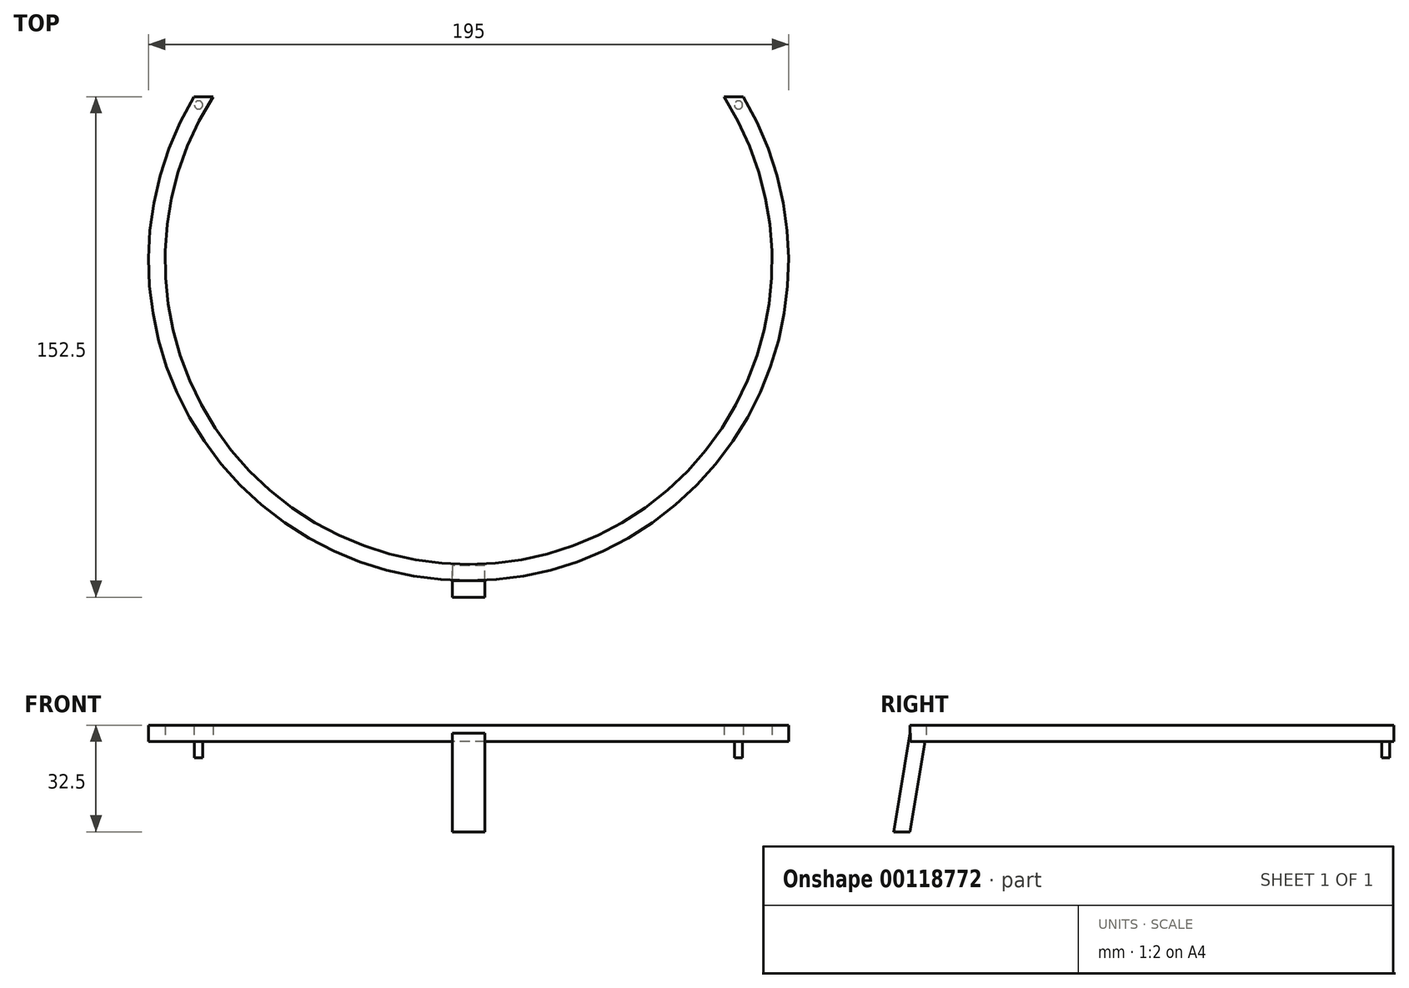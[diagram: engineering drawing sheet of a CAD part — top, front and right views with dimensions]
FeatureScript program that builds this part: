
annotation { "Feature Type Name" : "Feature", "Feature Type Description" : "" }
export const myFeature = defineFeature(function(context is Context, id is Id, definition is map)
    precondition{}
    {
        {
            var Q0;
            Q0=qCreatedBy(makeId("Top.planeOp"),FACE);
            var sketch = newSketch(context, id + "F0", { "sketchPlane" : qUnion([Q0])});
            skCircle(sketch, "E0", {"center": v(0, 0) * mm, "radius": 97.5 * mm});
            skCircle(sketch, "E1", {"center": v(0, 0) * mm, "radius": 92.5 * mm});
            skSolve(sketch);
        }
        {
            var Q0;
            Q0 = qSketchRegion(id + "F0", true);
            extrude(context, id + "F1", {"entities" : qUnion([Q0]), "depth" : 5 * mm});
        }
        {
            var Q0;
            Q0=qCreatedBy(makeId("Right.planeOp"),FACE);
            var sketch = newSketch(context, id + "F2", { "sketchPlane" : qUnion([Q0])});
            skPoint(sketch, "E2", {"position": v(-95, 2.5) * mm});
            skLineSegment(sketch, "E3", {"start": v(-95, 2.5) * mm, "end": v(-100, -27.5) * mm});
            skSolve(sketch);
        }
        {
            var Q0;
            Q0=sQuery(id+"F2.wireOp",VERTEX,"E3.end");
            var Q1;
            Q1=qCreatedBy(makeId("Top.planeOp"),FACE);
            cPlane(context, id + "F3", {"entities" : qUnion([Q0, Q1]), "cplaneType" : CPlaneType.PLANE_POINT, "offset" : 25 * mm, "width" : 150 * mm, "height" : 150 * mm});
        }
        {
            var Q0;
            Q0=qCreatedBy(id+"F3.planeOp",FACE);
            var sketch = newSketch(context, id + "F4", { "sketchPlane" : qUnion([Q0])});
            skPoint(sketch, "E4", {"position": v(0, -100) * mm});
            skLineSegment(sketch, "E5.bottom", {"start": v(5, -102.5) * mm, "end": v(-5, -102.5) * mm});
            skLineSegment(sketch, "E5.top", {"start": v(5, -97.5) * mm, "end": v(-5, -97.5) * mm});
            skLineSegment(sketch, "E5.left", {"start": v(5, -102.5) * mm, "end": v(5, -97.5) * mm});
            skLineSegment(sketch, "E5.right", {"start": v(-5, -102.5) * mm, "end": v(-5, -97.5) * mm});
            skSolve(sketch);
        }
        {
            var Q0;
            Q0=makeQuery(id+"F4.imprint","IMPRINT",FACE,{"disambiguationData":[TD([[makeQuery(id+"F4.imprint","IMPRINT",EDGE,{"derivedFrom":sQuery(id+"F4.wireOp",EDGE,"E5.bottom")}),-1.0]])]});
            var Q1;
            Q1=sQuery(id+"F2.wireOp",EDGE,"E3");
            sweep(context, id + "F5", {"operationType" : NewBodyOperationType.ADD, "profiles" : qUnion([Q0]), "path" : qUnion([Q1])});
        }
        {
            var Q0;
            Q0=makeQuery(id+"F1.opExtrude","CAP_FACE",FACE,{"disambiguationData":[OSD([sQuery(id+"F0.wireOp",EDGE,"E0"),sQuery(id+"F0.wireOp",EDGE,"E1")])],"isStart":true});
            var sketch = newSketch(context, id + "F6", { "sketchPlane" : qUnion([Q0])});
            skLineSegment(sketch, "E6", {"start": v(0, 0) * mm, "end": v(-74.69, -62.67) * mm});
            skLineSegment(sketch, "E7", {"start": v(0, 0) * mm, "end": v(-91.62, -33.35) * mm});
            skLineSegment(sketch, "E8.MirrorCS", {"start": v(0, 0) * mm, "end": v(74.69, -62.67) * mm});
            skLineSegment(sketch, "E9.MirrorCS", {"start": v(0, 0) * mm, "end": v(91.62, -33.35) * mm});
            skSolve(sketch);
        }
        {
            var Q0;
            {var subQ0=sQuery(id+"F6.wireOp",EDGE,"E6");var subQ1=makeQuery(id+"F1.opExtrude","CAP_EDGE",EDGE,{"disambiguationData":[OSD([sQuery(id+"F0.wireOp",EDGE,"E0")])],"isStart":true});var subQ2=makeQuery(id+"F6.imprint","INTERSECT",VERTEX,{"derivedFrom":[subQ1,subQ0]});Q0=makeQuery(id+"F6.imprint","IMPRINT",FACE,{"disambiguationData":[TD([[makeQuery(id+"F6.imprint","IMPRINT",EDGE,{"disambiguationData":[TD([[subQ2,1.0]])],"derivedFrom":subQ0}),-1.0]])]});}
            var Q1;
            {var subQ0=sQuery(id+"F6.wireOp",EDGE,"E8.MirrorCS");var subQ1=makeQuery(id+"F1.opExtrude","CAP_EDGE",EDGE,{"disambiguationData":[OSD([sQuery(id+"F0.wireOp",EDGE,"E0")])],"isStart":true});var subQ2=makeQuery(id+"F6.imprint","INTERSECT",VERTEX,{"derivedFrom":[subQ1,subQ0]});Q1=makeQuery(id+"F6.imprint","IMPRINT",FACE,{"disambiguationData":[TD([[makeQuery(id+"F6.imprint","IMPRINT",EDGE,{"disambiguationData":[TD([[subQ2,1.0]])],"derivedFrom":subQ0}),1.0]])]});}
            extrude(context, id + "F7", {"entities" : qUnion([Q0, Q1]), "operationType" : NewBodyOperationType.ADD, "depth" : 27.5 * mm});
        }
        {
            var Q0;
            Q0=qCreatedBy(makeId("Right.planeOp"),FACE);
            cPlane(context, id + "F8", {"entities" : qUnion([Q0]), "cplaneType" : CPlaneType.OFFSET, "offset" : 100 * mm, "width" : 150 * mm, "height" : 150 * mm});
        }
        {
            var Q0;
            Q0=qCreatedBy(id+"F8.planeOp",FACE);
            var sketch = newSketch(context, id + "F9", { "sketchPlane" : qUnion([Q0])});
            skLineSegment(sketch, "E10", {"start": v(0, 0) * mm, "end": v(50, 0) * mm});
            skLineSegment(sketch, "E11", {"start": v(50, 0) * mm, "end": v(50, 5) * mm});
            skLineSegment(sketch, "E12", {"start": v(50, 5) * mm, "end": v(101.86, 5) * mm});
            skLineSegment(sketch, "E13", {"start": v(101.86, 5) * mm, "end": v(101.86, -29.5) * mm});
            skLineSegment(sketch, "E14", {"start": v(101.86, -29.5) * mm, "end": v(0, -29.5) * mm});
            skLineSegment(sketch, "E15", {"start": v(0, -29.5) * mm, "end": v(0, 0) * mm});
            skLineSegment(sketch, "E16", {"start": v(50, 5) * mm, "end": v(-137.03, 5) * mm});
            skLineSegment(sketch, "E17", {"start": v(-137.03, 5) * mm, "end": v(-137.03, -29.5) * mm});
            skLineSegment(sketch, "E18", {"start": v(-137.03, -29.5) * mm, "end": v(0, -29.5) * mm});
            skSolve(sketch);
        }
        {
            var Q0;
            Q0=makeQuery(id+"F9.imprint","IMPRINT",FACE,{"disambiguationData":[TD([[makeQuery(id+"F9.imprint","IMPRINT",EDGE,{"derivedFrom":sQuery(id+"F9.wireOp",EDGE,"E10")}),-1.0]])]});
            extrude(context, id + "F10", {"entities" : qUnion([Q0]), "operationType" : NewBodyOperationType.REMOVE, "endBound" : BoundingType.THROUGH_ALL, "oppositeDirection" : true, "depth" : 25 * mm});
        }
        {
            var Q0;
            {var subQ2=sQuery(id+"F0.wireOp",EDGE,"E0");var subQ4=sQuery(id+"F6.wireOp",EDGE,"E7");var subQ6=sQuery(id+"F0.wireOp",EDGE,"E1");Q0=makeQuery(id+"F10.boolean.opBoolean","MERGE",FACE,{"derivedFrom":[makeQuery(id+"F7.boolean.opBoolean","SPLIT",FACE,{"disambiguationData":[TD([makeQuery(id+"F7.opExtrude","SWEPT_FACE",FACE,{"disambiguationData":[OSD([subQ4])]})])],"derivedFrom":makeQuery(id+"F1.opExtrude","CAP_FACE",FACE,{"disambiguationData":[OSD([subQ2,subQ6])],"isStart":true})}),makeQuery(id+"F10.opExtrude","SWEPT_FACE",FACE,{"disambiguationData":[OSD([sQuery(id+"F9.wireOp",EDGE,"E10")])]})]});}
            var sketch = newSketch(context, id + "F11", { "sketchPlane" : qUnion([Q0])});
            skPoint(sketch, "E19", {"position": v(82.26, -47.5) * mm});
            skLineSegment(sketch, "E20", {"start": v(85.15, -47.5) * mm, "end": v(79.37, -47.5) * mm, "construction": true});
            skCircle(sketch, "E21", {"center": v(82.26, -47.5) * mm, "radius": 1.25 * mm});
            skCircle(sketch, "E22.MirrorC", {"center": v(-82.26, -47.5) * mm, "radius": 1.25 * mm});
            skSolve(sketch);
        }
        {
            var Q0;
            Q0 = qSketchRegion(id + "F11", true);
            extrude(context, id + "F12", {"entities" : qUnion([Q0]), "operationType" : NewBodyOperationType.ADD, "depth" : 5 * mm});
        }
    });
